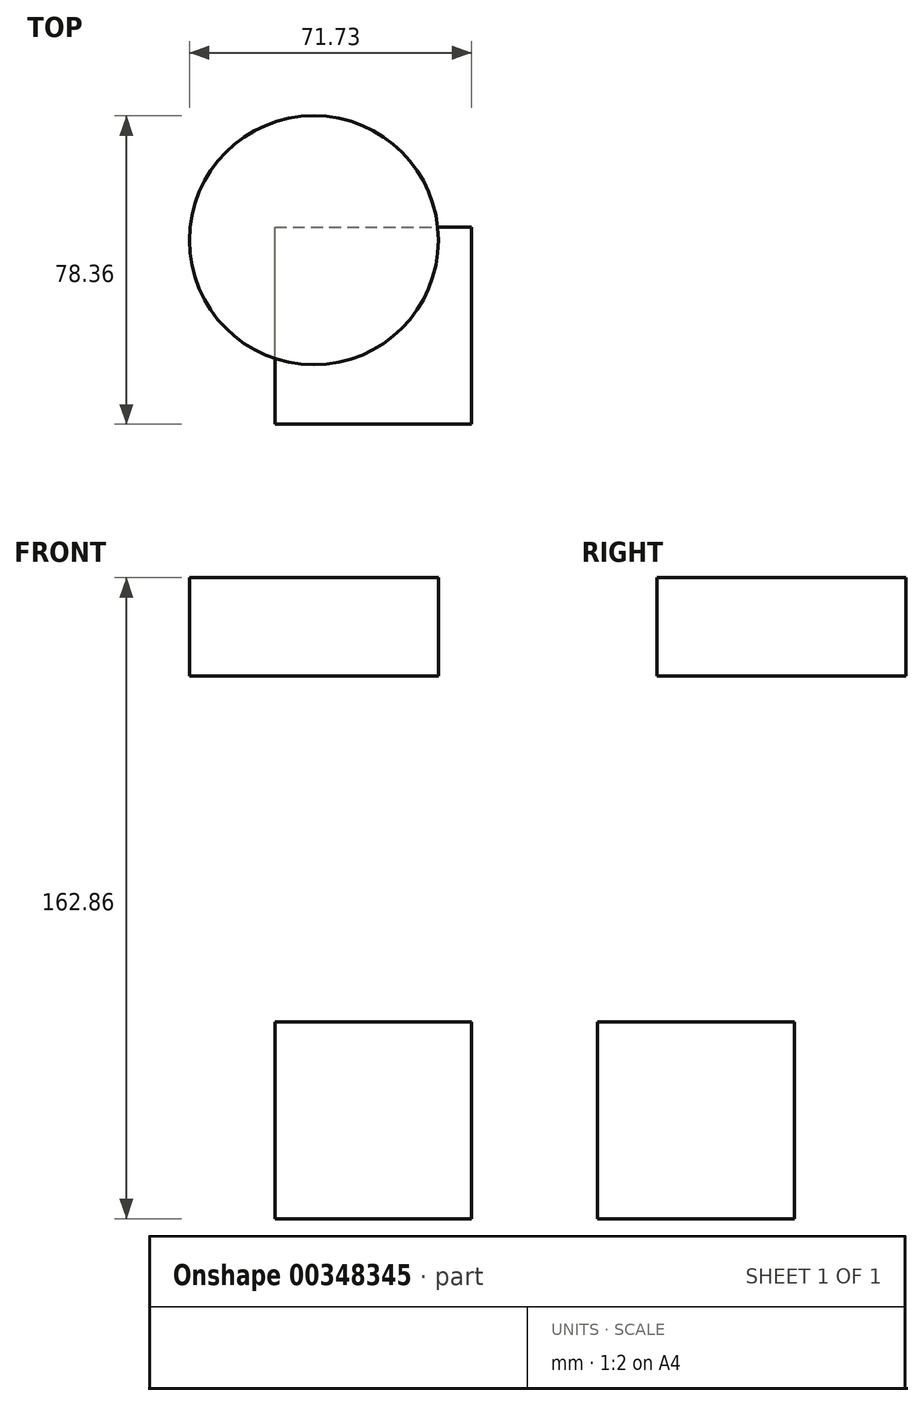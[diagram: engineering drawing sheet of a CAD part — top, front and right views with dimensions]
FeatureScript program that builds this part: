
annotation { "Feature Type Name" : "Feature", "Feature Type Description" : "" }
export const myFeature = defineFeature(function(context is Context, id is Id, definition is map)
    precondition{}
    {
        {
            var Q0;
            Q0=qCreatedBy(makeId("Front.planeOp"),FACE);
            var sketch = newSketch(context, id + "F0", { "sketchPlane" : qUnion([Q0])});
            skLineSegment(sketch, "E0.bottom", {"start": v(-13.16, 12.14) * mm, "end": v(36.84, 12.14) * mm});
            skLineSegment(sketch, "E0.top", {"start": v(-13.16, -37.86) * mm, "end": v(36.84, -37.86) * mm});
            skLineSegment(sketch, "E0.left", {"start": v(-13.16, 12.14) * mm, "end": v(-13.16, -37.86) * mm});
            skLineSegment(sketch, "E0.right", {"start": v(36.84, 12.14) * mm, "end": v(36.84, -37.86) * mm});
            skSolve(sketch);
        }
        {
            var Q0;
            Q0=makeQuery(id+"F0.imprint","IMPRINT",FACE,{"disambiguationData":[TD([[makeQuery(id+"F0.imprint","IMPRINT",EDGE,{"derivedFrom":sQuery(id+"F0.wireOp",EDGE,"E0.bottom")}),-1.0]])]});
            extrude(context, id + "F1", {"entities" : qUnion([Q0]), "depth" : 50 * mm});
        }
        {
            var Q0;
            Q0=qCreatedBy(makeId("Top.planeOp"),FACE);
            cPlane(context, id + "F2", {"entities" : qUnion([Q0]), "cplaneType" : CPlaneType.OFFSET, "offset" : 100 * mm, "width" : 150 * mm, "height" : 150 * mm});
        }
        {
            var Q0;
            Q0=qCreatedBy(id+"F2.planeOp",FACE);
            var sketch = newSketch(context, id + "F3", { "sketchPlane" : qUnion([Q0])});
            skCircle(sketch, "E1", {"center": v(-3.26, -3.27) * mm, "radius": 31.63 * mm});
            skSolve(sketch);
        }
        {
            var Q0;
            Q0 = qSketchRegion(id + "F3", true);
            extrude(context, id + "F4", {"entities" : qUnion([Q0]), "depth" : 25 * mm});
        }
    });
